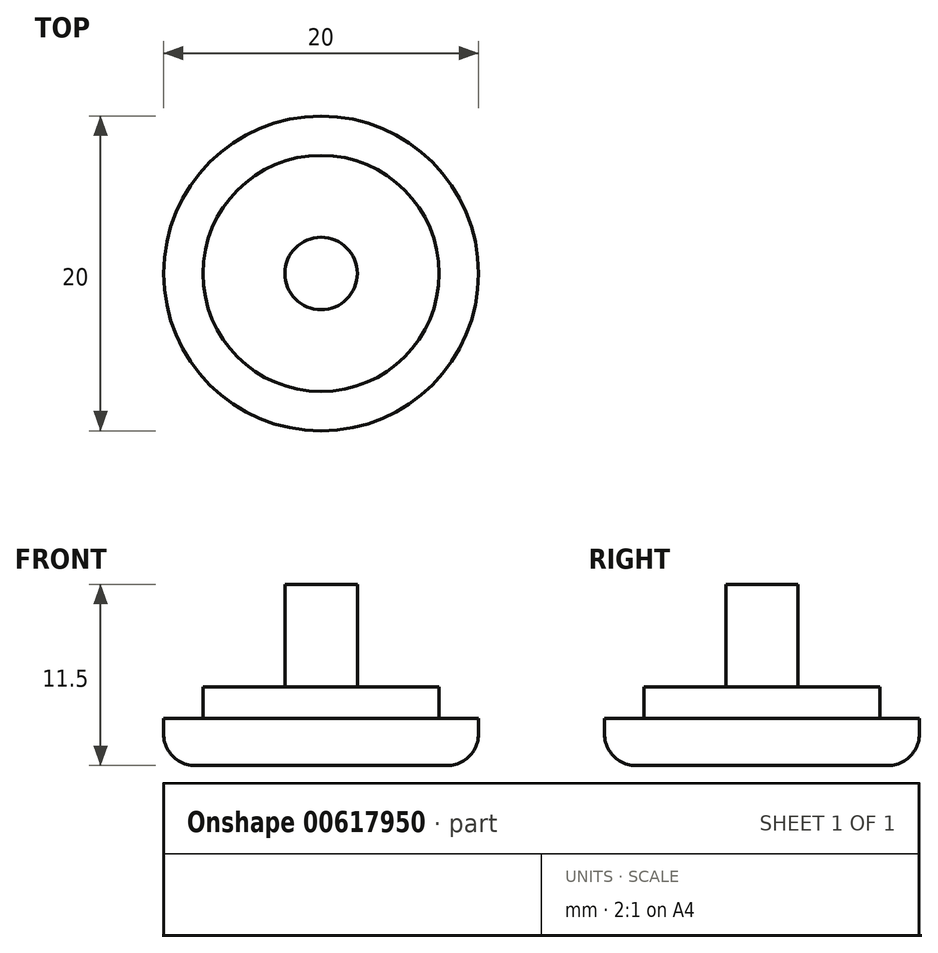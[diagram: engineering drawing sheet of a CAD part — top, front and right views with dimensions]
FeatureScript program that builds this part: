
annotation { "Feature Type Name" : "Feature", "Feature Type Description" : "" }
export const myFeature = defineFeature(function(context is Context, id is Id, definition is map)
    precondition{}
    {
        {
            var Q0;
            Q0=qCreatedBy(makeId("Top.planeOp"),FACE);
            var sketch = newSketch(context, id + "F0", { "sketchPlane" : qUnion([Q0])});
            skCircle(sketch, "E0", {"center": v(0, 0) * mm, "radius": 10 * mm});
            skSolve(sketch);
        }
        {
            var Q0;
            Q0=makeQuery(id+"F0.imprint","IMPRINT",FACE,{"disambiguationData":[TD([[makeQuery(id+"F0.imprint","IMPRINT",EDGE,{"derivedFrom":sQuery(id+"F0.wireOp",EDGE,"E0")}),1.0]])]});
            extrude(context, id + "F1", {"entities" : qUnion([Q0]), "depth" : 3 * mm, "offsetDistance" : 25 * mm});
        }
        {
            var Q0;
            Q0=makeQuery(id+"F1.opExtrude","CAP_EDGE",EDGE,{"disambiguationData":[OSD([sQuery(id+"F0.wireOp",EDGE,"E0")])],"isStart":true});
            fillet(context, id + "F2", {"entities" : qUnion([Q0]), "radius" : 2 * mm, "tangentPropagation" : true, "allowEdgeOverflow" : false});
        }
        {
            var Q0;
            Q0=makeQuery(id+"F1.opExtrude","CAP_FACE",FACE,{"disambiguationData":[OSD([sQuery(id+"F0.wireOp",EDGE,"E0")])],"isStart":false});
            var sketch = newSketch(context, id + "F3", { "sketchPlane" : qUnion([Q0])});
            skCircle(sketch, "E1", {"center": v(0, 0) * mm, "radius": 7.5 * mm});
            skSolve(sketch);
        }
        {
            var Q0;
            Q0 = qSketchRegion(id + "F3", true);
            extrude(context, id + "F4", {"entities" : qUnion([Q0]), "operationType" : NewBodyOperationType.ADD, "depth" : 2 * mm, "offsetDistance" : 25 * mm});
        }
        {
            var Q0;
            Q0=makeQuery(id+"F4.opExtrude","CAP_FACE",FACE,{"disambiguationData":[OSD([sQuery(id+"F3.wireOp",EDGE,"E1")])],"isStart":false});
            var sketch = newSketch(context, id + "F5", { "sketchPlane" : qUnion([Q0])});
            skCircle(sketch, "E2", {"center": v(0, 0) * mm, "radius": 2.3 * mm});
            skSolve(sketch);
        }
        {
            var Q0;
            Q0=makeQuery(id+"F5.imprint","IMPRINT",FACE,{"disambiguationData":[TD([[makeQuery(id+"F5.imprint","IMPRINT",EDGE,{"derivedFrom":sQuery(id+"F5.wireOp",EDGE,"E2")}),1.0]])]});
            extrude(context, id + "F6", {"entities" : qUnion([Q0]), "operationType" : NewBodyOperationType.ADD, "depth" : 6.5 * mm, "offsetDistance" : 25 * mm});
        }
    });
